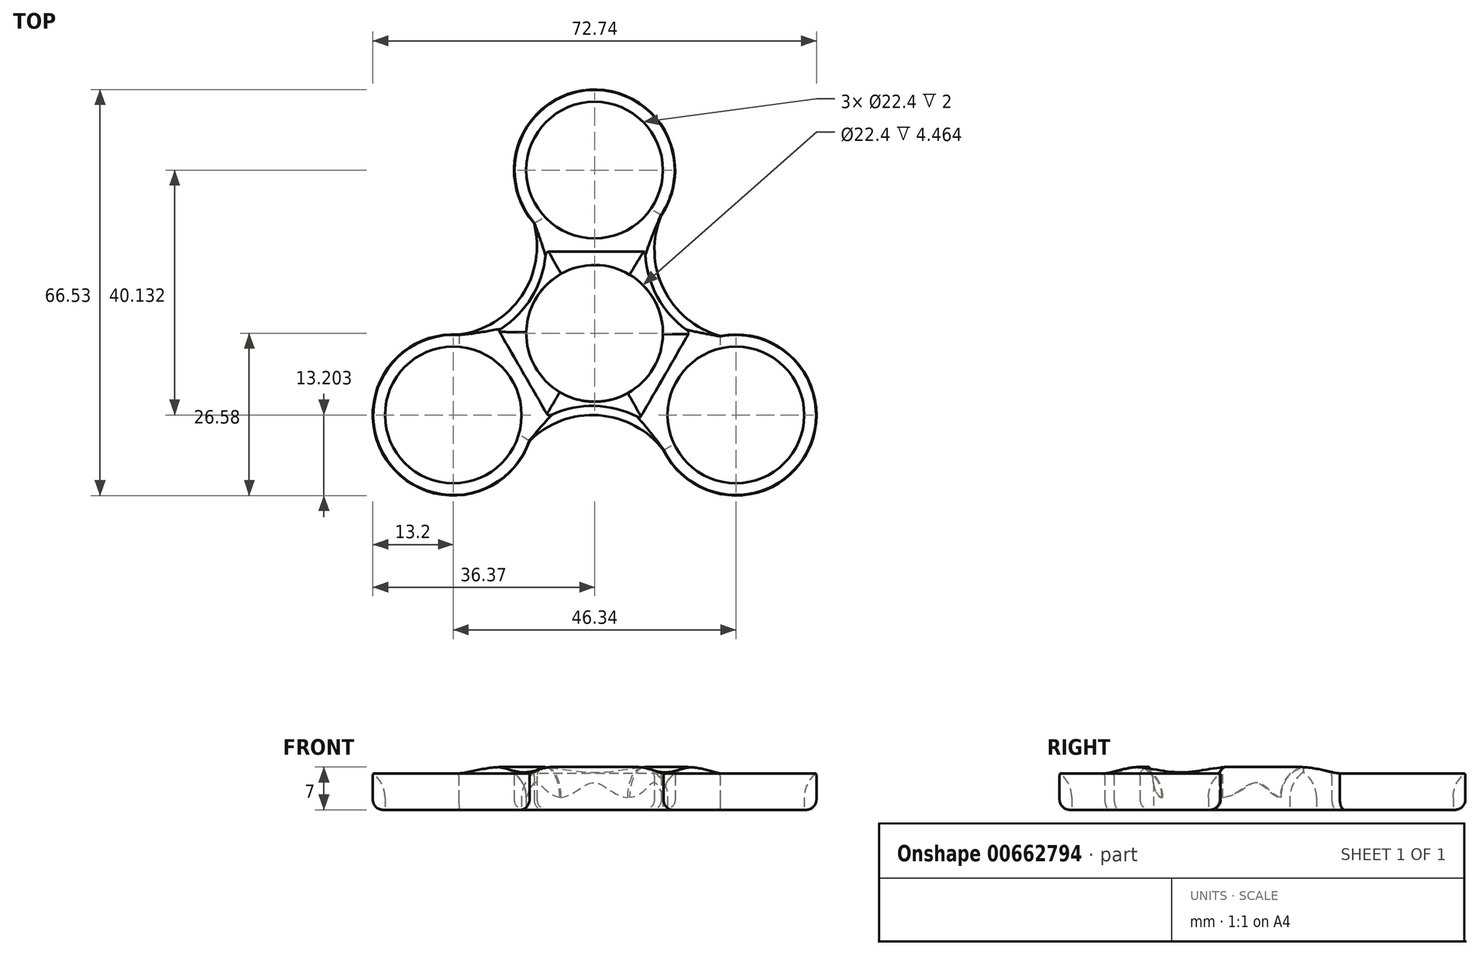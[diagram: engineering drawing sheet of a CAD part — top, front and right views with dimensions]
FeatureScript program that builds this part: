
annotation { "Feature Type Name" : "Feature", "Feature Type Description" : "" }
export const myFeature = defineFeature(function(context is Context, id is Id, definition is map)
    precondition{}
    {
        {
            var Q0;
            Q0=qCreatedBy(makeId("Top.planeOp"),FACE);
            var sketch = newSketch(context, id + "F0", { "sketchPlane" : qUnion([Q0])});
            skCircle(sketch, "E0", {"center": v(0, 0) * mm, "radius": 11.2 * mm});
            skCircle(sketch, "E1", {"center": v(0, 26.75) * mm, "radius": 11.2 * mm});
            skArc(sketch, "E2", {"start": v(10.95, 19.38) * mm, "mid": v(-0.83, 39.93) * mm, "end": v(-9.93, 18.06) * mm});
            skCircle(sketch, "E3.1.0", {"center": v(-23.17, -13.38) * mm, "radius": 11.2 * mm});
            skCircle(sketch, "E3.2.0", {"center": v(23.17, -13.38) * mm, "radius": 11.2 * mm});
            skArc(sketch, "E4", {"start": v(-22.26, -0.2) * mm, "mid": v(-34.16, -20.69) * mm, "end": v(-10.67, -17.63) * mm});
            skArc(sketch, "E5", {"start": v(11.3, -19.17) * mm, "mid": v(35, -19.24) * mm, "end": v(20.6, -0.43) * mm});
            skArc(sketch, "E6", {"start": v(10.95, 19.38) * mm, "mid": v(11.3, 7.3) * mm, "end": v(20.6, -0.43) * mm});
            skArc(sketch, "E7.1.0", {"start": v(-22.26, -0.2) * mm, "mid": v(-11.96, 6.14) * mm, "end": v(-9.93, 18.06) * mm});
            skArc(sketch, "E7.2.0", {"start": v(11.3, -19.17) * mm, "mid": v(0.67, -13.43) * mm, "end": v(-10.67, -17.63) * mm});
            skSolve(sketch);
        }
        {
            var Q0;
            Q0=makeQuery(id+"F0.imprint","IMPRINT",FACE,{"disambiguationData":[TD([[makeQuery(id+"F0.imprint","IMPRINT",EDGE,{"derivedFrom":sQuery(id+"F0.wireOp",EDGE,"E0")}),-1.0]])]});
            extrude(context, id + "F1", {"entities" : qUnion([Q0]), "depth" : 7 * mm, "offsetDistance" : 25 * mm});
        }
        {
            var Q0;
            Q0=makeQuery(id+"F1.opExtrude","CAP_EDGE",EDGE,{"disambiguationData":[OSD([sQuery(id+"F0.wireOp",EDGE,"E6")])],"isStart":false});
            var Q1;
            Q1=makeQuery(id+"F1.opExtrude","CAP_EDGE",EDGE,{"disambiguationData":[OSD([sQuery(id+"F0.wireOp",EDGE,"E5")])],"isStart":false});
            var Q2;
            Q2=makeQuery(id+"F1.opExtrude","CAP_EDGE",EDGE,{"disambiguationData":[OSD([sQuery(id+"F0.wireOp",EDGE,"E7.2.0")])],"isStart":false});
            var Q3;
            Q3=makeQuery(id+"F1.opExtrude","CAP_EDGE",EDGE,{"disambiguationData":[OSD([sQuery(id+"F0.wireOp",EDGE,"E4")])],"isStart":false});
            var Q4;
            Q4=makeQuery(id+"F1.opExtrude","CAP_EDGE",EDGE,{"disambiguationData":[OSD([sQuery(id+"F0.wireOp",EDGE,"E7.1.0")])],"isStart":false});
            var Q5;
            Q5=makeQuery(id+"F1.opExtrude","CAP_EDGE",EDGE,{"disambiguationData":[OSD([sQuery(id+"F0.wireOp",EDGE,"E2")])],"isStart":false});
            fillet(context, id + "F2", {"entities" : qUnion([Q0, Q1, Q2, Q3, Q4, Q5]), "radius" : 1.5 * mm, "tangentPropagation" : true, "allowEdgeOverflow" : false});
        }
        {
            var Q0;
            Q0=makeQuery(id+"F1.opExtrude","CAP_EDGE",EDGE,{"disambiguationData":[OSD([sQuery(id+"F0.wireOp",EDGE,"E6")])],"isStart":true});
            var Q1;
            Q1=makeQuery(id+"F1.opExtrude","CAP_EDGE",EDGE,{"disambiguationData":[OSD([sQuery(id+"F0.wireOp",EDGE,"E5")])],"isStart":true});
            var Q2;
            Q2=makeQuery(id+"F1.opExtrude","CAP_EDGE",EDGE,{"disambiguationData":[OSD([sQuery(id+"F0.wireOp",EDGE,"E2")])],"isStart":true});
            var Q3;
            Q3=makeQuery(id+"F1.opExtrude","CAP_EDGE",EDGE,{"disambiguationData":[OSD([sQuery(id+"F0.wireOp",EDGE,"E7.1.0")])],"isStart":true});
            var Q4;
            Q4=makeQuery(id+"F1.opExtrude","CAP_EDGE",EDGE,{"disambiguationData":[OSD([sQuery(id+"F0.wireOp",EDGE,"E4")])],"isStart":true});
            var Q5;
            Q5=makeQuery(id+"F1.opExtrude","CAP_EDGE",EDGE,{"disambiguationData":[OSD([sQuery(id+"F0.wireOp",EDGE,"E7.2.0")])],"isStart":true});
            fillet(context, id + "F3", {"entities" : qUnion([Q0, Q1, Q2, Q3, Q4, Q5]), "radius" : 1.7 * mm, "tangentPropagation" : true, "allowEdgeOverflow" : false});
        }
        {
            var Q0;
            Q0=makeQuery(id+"F1.opExtrude","CAP_FACE",FACE,{"disambiguationData":[OSD([sQuery(id+"F0.wireOp",EDGE,"E0"),sQuery(id+"F0.wireOp",EDGE,"E1"),sQuery(id+"F0.wireOp",EDGE,"E2"),sQuery(id+"F0.wireOp",EDGE,"E3.1.0"),sQuery(id+"F0.wireOp",EDGE,"E3.2.0"),sQuery(id+"F0.wireOp",EDGE,"E4"),sQuery(id+"F0.wireOp",EDGE,"E5"),sQuery(id+"F0.wireOp",EDGE,"E6"),sQuery(id+"F0.wireOp",EDGE,"E7.1.0"),sQuery(id+"F0.wireOp",EDGE,"E7.2.0")])],"isStart":false});
            fillet(context, id + "F4", {"entities" : qUnion([Q0]), "radius" : 5 * mm, "tangentPropagation" : true, "allowEdgeOverflow" : false});
        }
    });
